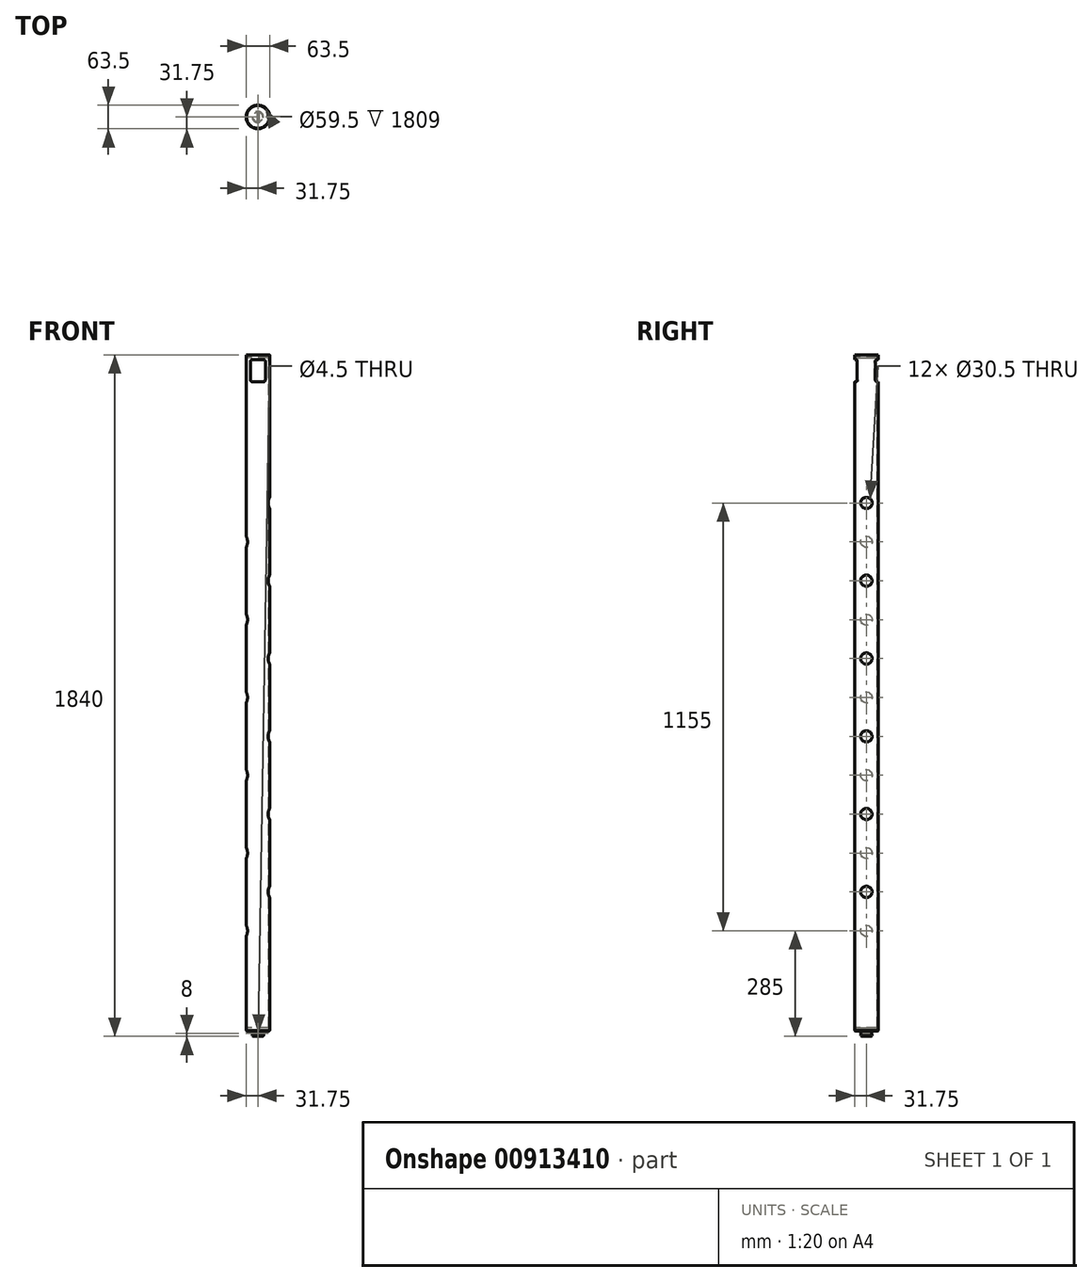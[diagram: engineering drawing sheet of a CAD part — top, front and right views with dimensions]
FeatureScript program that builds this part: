
annotation { "Feature Type Name" : "Feature", "Feature Type Description" : "" }
export const myFeature = defineFeature(function(context is Context, id is Id, definition is map)
    precondition{}
    {
        {
            var Q0;
            Q0=qCreatedBy(makeId("Right.planeOp"),FACE);
            var sketch = newSketch(context, id + "F0", { "sketchPlane" : qUnion([Q0])});
            skLineSegment(sketch, "E0", {"start": v(0, 964.83) * mm, "end": v(0, -949.23) * mm, "construction": true});
            skLineSegment(sketch, "E1", {"start": v(-273.12, 0) * mm, "end": v(405.48, 0) * mm, "construction": true});
            skLineSegment(sketch, "E2.0", {"start": v(0, 920) * mm, "end": v(31.75, 920) * mm});
            skLineSegment(sketch, "E3.0", {"start": v(0, -920) * mm, "end": v(15, -920) * mm});
            skLineSegment(sketch, "E4.0", {"start": v(31.75, 920) * mm, "end": v(31.75, -905) * mm});
            skLineSegment(sketch, "E5", {"start": v(15, -920) * mm, "end": v(15, -905) * mm});
            skLineSegment(sketch, "E6", {"start": v(15, -905) * mm, "end": v(31.75, -905) * mm});
            skLineSegment(sketch, "E7", {"start": v(0, -897) * mm, "end": v(29.75, -897) * mm});
            skLineSegment(sketch, "E8.0", {"start": v(29.75, 912) * mm, "end": v(29.75, -897) * mm});
            skLineSegment(sketch, "E9.filletArc", {"start": v(15, -920) * mm, "end": v(15, -920) * mm});
            skLineSegment(sketch, "E10.0", {"start": v(0, 912) * mm, "end": v(29.75, 912) * mm});
            skLineSegment(sketch, "E11.filletArc", {"start": v(29.75, 912) * mm, "end": v(29.75, 912) * mm});
            skLineSegment(sketch, "E12.filletArc", {"start": v(31.75, 920) * mm, "end": v(31.75, 920) * mm});
            skLineSegment(sketch, "E13", {"start": v(0, 920) * mm, "end": v(0, 912) * mm});
            skLineSegment(sketch, "E14", {"start": v(0, -897) * mm, "end": v(0, -920) * mm});
            skSolve(sketch);
        }
        {
            var Q0;
            Q0=makeQuery(id+"F0.imprint","IMPRINT",FACE,{"disambiguationData":[TD([[makeQuery(id+"F0.imprint","IMPRINT",EDGE,{"derivedFrom":sQuery(id+"F0.wireOp",EDGE,"E2.0")}),-1.0]])]});
            var Q1;
            Q1=sQuery(id+"F0.wireOp",EDGE,"E0");
            revolve(context, id + "F1", {"surfaceOperationType" : NewSurfaceOperationType.NEW, "entities" : qUnion([Q0]), "axis" : qUnion([Q1]), "revolveType" : RevolveType.FULL});
        }
        {
            var Q0;
            Q0=makeQuery(id+"F1.opRevolve","SWEPT_EDGE",EDGE,{"disambiguationData":[OSD([sQuery(id+"F0.wireOp",EDGE,"E2.0"),sQuery(id+"F0.wireOp",EDGE,"E4.0")])]});
            var Q1;
            Q1=makeQuery(id+"F1.opRevolve","SWEPT_EDGE",EDGE,{"disambiguationData":[OSD([sQuery(id+"F0.wireOp",EDGE,"E4.0"),sQuery(id+"F0.wireOp",EDGE,"E6")])]});
            chamfer(context, id + "F2", {"entities" : qUnion([Q0, Q1]), "width" : 1 * mm, "tangentPropagation" : true});
        }
        {
            var Q0;
            Q0=makeQuery(id+"F1.opRevolve","SWEPT_EDGE",EDGE,{"disambiguationData":[OSD([sQuery(id+"F0.wireOp",EDGE,"E3.0"),sQuery(id+"F0.wireOp",EDGE,"E5")])]});
            chamfer(context, id + "F3", {"entities" : qUnion([Q0]), "width" : 2 * mm, "tangentPropagation" : true});
        }
        {
            var Q0;
            Q0=qCreatedBy(makeId("Front.planeOp"),FACE);
            var sketch = newSketch(context, id + "F4", { "sketchPlane" : qUnion([Q0])});
            skLineSegment(sketch, "E15.0", {"start": v(-15, 907) * mm, "end": v(15, 907) * mm});
            skLineSegment(sketch, "E16.0", {"start": v(-15, 847) * mm, "end": v(15, 847) * mm});
            skLineSegment(sketch, "E17", {"start": v(0, 933.17) * mm, "end": v(0, 804.26) * mm, "construction": true});
            skLineSegment(sketch, "E18.0", {"start": v(20, 902) * mm, "end": v(20, 852) * mm});
            skLineSegment(sketch, "E19.MirrorCS", {"start": v(-20, 902) * mm, "end": v(-20, 852) * mm});
            skPoint(sketch, "E20.newPointB", {"position": v(20, 933.17) * mm});
            skArc(sketch, "E20.filletArc", {"start": v(20, 902) * mm, "mid": v(18.54, 905.54) * mm, "end": v(15, 907) * mm});
            skPoint(sketch, "E21.newPointA", {"position": v(-20, 933.17) * mm});
            skArc(sketch, "E21.filletArc", {"start": v(-15, 907) * mm, "mid": v(-18.54, 905.54) * mm, "end": v(-20, 902) * mm});
            skPoint(sketch, "E22.newPointA", {"position": v(-20, 804.26) * mm});
            skArc(sketch, "E22.filletArc", {"start": v(-20, 852) * mm, "mid": v(-18.54, 848.46) * mm, "end": v(-15, 847) * mm});
            skPoint(sketch, "E23.newPointB", {"position": v(20, 804.26) * mm});
            skArc(sketch, "E23.filletArc", {"start": v(15, 847) * mm, "mid": v(18.54, 848.46) * mm, "end": v(20, 852) * mm});
            skLineSegment(sketch, "E24.0", {"start": v(13, -912) * mm, "end": v(-13, -912) * mm, "construction": true});
            skCircle(sketch, "E25", {"center": v(0, -912) * mm, "radius": 2.25 * mm});
            skSolve(sketch);
        }
        {
            var Q0;
            Q0=makeQuery(id+"F4.imprint","IMPRINT",FACE,{"disambiguationData":[TD([[makeQuery(id+"F4.imprint","IMPRINT",EDGE,{"derivedFrom":sQuery(id+"F4.wireOp",EDGE,"E15.0")}),-1.0]])]});
            extrude(context, id + "F5", {"entities" : qUnion([Q0]), "operationType" : NewBodyOperationType.REMOVE, "endBound" : BoundingType.SYMMETRIC, "depth" : 100 * mm, "offsetDistance" : 25 * mm});
        }
        {
            var Q0;
            Q0=qCreatedBy(makeId("Right.planeOp"),FACE);
            var sketch = newSketch(context, id + "F6", { "sketchPlane" : qUnion([Q0])});
            skLineSegment(sketch, "E26.0", {"start": v(-144.84, 920) * mm, "end": v(213, 920) * mm, "construction": true});
            skLineSegment(sketch, "E27.0", {"start": v(-144.84, 520) * mm, "end": v(213, 520) * mm, "construction": true});
            skLineSegment(sketch, "E28.direction1", {"start": v(-144.84, 520) * mm, "end": v(-119.84, 520) * mm, "construction": true});
            skLineSegment(sketch, "E29", {"start": v(0, 984.2) * mm, "end": v(0, -983.92) * mm, "construction": true});
            skCircle(sketch, "E30", {"center": v(0, 520) * mm, "radius": 15.25 * mm});
            skCircle(sketch, "E31.0.1.0", {"center": v(0, 415) * mm, "radius": 15.25 * mm});
            skCircle(sketch, "E31.0.2.0", {"center": v(0, 310) * mm, "radius": 15.25 * mm});
            skCircle(sketch, "E31.0.3.0", {"center": v(0, 205) * mm, "radius": 15.25 * mm});
            skCircle(sketch, "E31.0.4.0", {"center": v(0, 100) * mm, "radius": 15.25 * mm});
            skCircle(sketch, "E31.0.5.0", {"center": v(0, -5) * mm, "radius": 15.25 * mm});
            skCircle(sketch, "E31.0.6.0", {"center": v(0, -110) * mm, "radius": 15.25 * mm});
            skCircle(sketch, "E31.0.7.0", {"center": v(0, -215) * mm, "radius": 15.25 * mm});
            skCircle(sketch, "E31.0.8.0", {"center": v(0, -320) * mm, "radius": 15.25 * mm});
            skCircle(sketch, "E31.0.9.0", {"center": v(0, -425) * mm, "radius": 15.25 * mm});
            skCircle(sketch, "E31.0.10.0", {"center": v(0, -530) * mm, "radius": 15.25 * mm});
            skCircle(sketch, "E31.0.11.0", {"center": v(0, -635) * mm, "radius": 15.25 * mm});
            skLineSegment(sketch, "E31.direction1", {"start": v(0, 520) * mm, "end": v(25, 520) * mm, "construction": true});
            skLineSegment(sketch, "E31.direction2", {"start": v(0, 520) * mm, "end": v(0, 415) * mm, "construction": true});
            skSolve(sketch);
        }
        {
            var Q0;
            Q0=makeQuery(id+"F6.imprint","IMPRINT",FACE,{"disambiguationData":[TD([[makeQuery(id+"F6.imprint","IMPRINT",EDGE,{"derivedFrom":sQuery(id+"F6.wireOp",EDGE,"E30")}),1.0]])]});
            var Q1;
            Q1=makeQuery(id+"F6.imprint","IMPRINT",FACE,{"disambiguationData":[TD([[makeQuery(id+"F6.imprint","IMPRINT",EDGE,{"derivedFrom":sQuery(id+"F6.wireOp",EDGE,"E31.0.2.0")}),1.0]])]});
            var Q2;
            Q2=makeQuery(id+"F6.imprint","IMPRINT",FACE,{"disambiguationData":[TD([[makeQuery(id+"F6.imprint","IMPRINT",EDGE,{"derivedFrom":sQuery(id+"F6.wireOp",EDGE,"E31.0.4.0")}),1.0]])]});
            var Q3;
            Q3=makeQuery(id+"F6.imprint","IMPRINT",FACE,{"disambiguationData":[TD([[makeQuery(id+"F6.imprint","IMPRINT",EDGE,{"derivedFrom":sQuery(id+"F6.wireOp",EDGE,"E31.0.6.0")}),1.0]])]});
            var Q4;
            Q4=makeQuery(id+"F6.imprint","IMPRINT",FACE,{"disambiguationData":[TD([[makeQuery(id+"F6.imprint","IMPRINT",EDGE,{"derivedFrom":sQuery(id+"F6.wireOp",EDGE,"E31.0.8.0")}),1.0]])]});
            var Q5;
            Q5=makeQuery(id+"F6.imprint","IMPRINT",FACE,{"disambiguationData":[TD([[makeQuery(id+"F6.imprint","IMPRINT",EDGE,{"derivedFrom":sQuery(id+"F6.wireOp",EDGE,"E31.0.10.0")}),1.0]])]});
            extrude(context, id + "F7", {"entities" : qUnion([Q0, Q1, Q2, Q3, Q4, Q5]), "operationType" : NewBodyOperationType.REMOVE, "depth" : 50 * mm, "offsetDistance" : 25 * mm});
        }
        {
            var Q0;
            Q0=makeQuery(id+"F6.imprint","IMPRINT",FACE,{"disambiguationData":[TD([[makeQuery(id+"F6.imprint","IMPRINT",EDGE,{"derivedFrom":sQuery(id+"F6.wireOp",EDGE,"E31.0.1.0")}),1.0]])]});
            var Q1;
            Q1=makeQuery(id+"F6.imprint","IMPRINT",FACE,{"disambiguationData":[TD([[makeQuery(id+"F6.imprint","IMPRINT",EDGE,{"derivedFrom":sQuery(id+"F6.wireOp",EDGE,"E31.0.3.0")}),1.0]])]});
            var Q2;
            Q2=makeQuery(id+"F6.imprint","IMPRINT",FACE,{"disambiguationData":[TD([[makeQuery(id+"F6.imprint","IMPRINT",EDGE,{"derivedFrom":sQuery(id+"F6.wireOp",EDGE,"E31.0.5.0")}),1.0]])]});
            var Q3;
            Q3=makeQuery(id+"F6.imprint","IMPRINT",FACE,{"disambiguationData":[TD([[makeQuery(id+"F6.imprint","IMPRINT",EDGE,{"derivedFrom":sQuery(id+"F6.wireOp",EDGE,"E31.0.7.0")}),1.0]])]});
            var Q4;
            Q4=makeQuery(id+"F6.imprint","IMPRINT",FACE,{"disambiguationData":[TD([[makeQuery(id+"F6.imprint","IMPRINT",EDGE,{"derivedFrom":sQuery(id+"F6.wireOp",EDGE,"E31.0.9.0")}),1.0]])]});
            var Q5;
            Q5=makeQuery(id+"F6.imprint","IMPRINT",FACE,{"disambiguationData":[TD([[makeQuery(id+"F6.imprint","IMPRINT",EDGE,{"derivedFrom":sQuery(id+"F6.wireOp",EDGE,"E31.0.11.0")}),1.0]])]});
            extrude(context, id + "F8", {"entities" : qUnion([Q0, Q1, Q2, Q3, Q4, Q5]), "operationType" : NewBodyOperationType.REMOVE, "oppositeDirection" : true, "depth" : 50 * mm, "offsetDistance" : 25 * mm});
        }
        {
            var Q0;
            Q0=makeQuery(id+"F4.imprint","IMPRINT",FACE,{"disambiguationData":[TD([[makeQuery(id+"F4.imprint","IMPRINT",EDGE,{"derivedFrom":sQuery(id+"F4.wireOp",EDGE,"E25")}),1.0]])]});
            extrude(context, id + "F9", {"entities" : qUnion([Q0]), "operationType" : NewBodyOperationType.REMOVE, "endBound" : BoundingType.SYMMETRIC, "oppositeDirection" : true, "depth" : 30 * mm, "offsetDistance" : 25 * mm});
        }
        {
            var Q0;
            Q0=makeQuery(id+"F9.boolean.opBoolean","INTERSECT",EDGE,{"disambiguationData":[OD(0.0)],"derivedFrom":[makeQuery(id+"F1.opRevolve","SWEPT_FACE",FACE,{"disambiguationData":[OSD([sQuery(id+"F0.wireOp",EDGE,"E5")])]}),makeQuery(id+"F9.opExtrude","SWEPT_FACE",FACE,{"disambiguationData":[OSD([sQuery(id+"F4.wireOp",EDGE,"E25")])]})]});
            var Q1;
            Q1=makeQuery(id+"F9.boolean.opBoolean","INTERSECT",EDGE,{"disambiguationData":[OD(1.0)],"derivedFrom":[makeQuery(id+"F1.opRevolve","SWEPT_FACE",FACE,{"disambiguationData":[OSD([sQuery(id+"F0.wireOp",EDGE,"E5")])]}),makeQuery(id+"F9.opExtrude","SWEPT_FACE",FACE,{"disambiguationData":[OSD([sQuery(id+"F4.wireOp",EDGE,"E25")])]})]});
            chamfer(context, id + "F10", {"entities" : qUnion([Q0, Q1]), "width" : 1 * mm, "tangentPropagation" : true});
        }
    });
